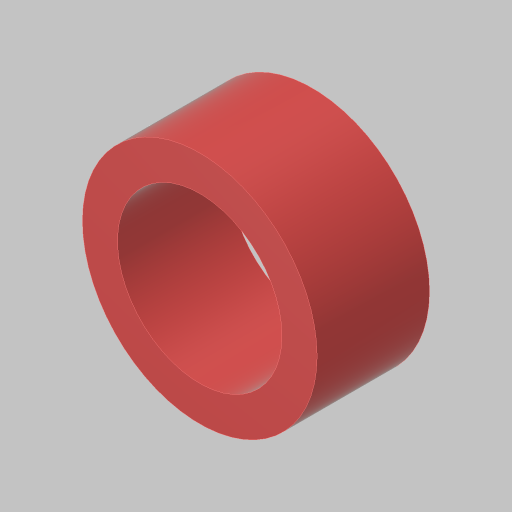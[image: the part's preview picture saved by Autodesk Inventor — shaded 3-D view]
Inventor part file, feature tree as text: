
AUTODESK INVENTOR PART (.ipt)
format: ipt  version: 2023.5 (Build 275446000, 446)  size: 114,688 bytes
history: native  units: in
note: dims shown in document units (in); Inventor stores cm internally (conversion verified against a paired STEP export)
features: extrude x1, sketch x1
ambient origin geometry x8: Origin, YZ Plane, XZ Plane, XY Plane, X Axis, Y Axis, Z Axis, Center Point
bodies: Solid1 (feature_tree)
feature tree (2):
  extrude  "Extrusion1"  Depth=0.4in
  sketch  "Sketch1"  dims[d0=0.585in d1=0.125in d2=0.4in d3=0.0in]
